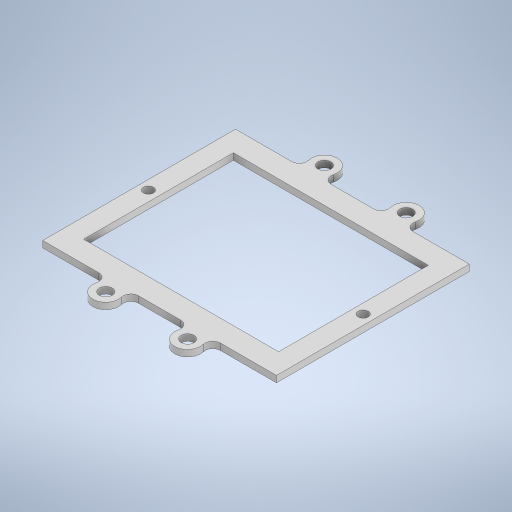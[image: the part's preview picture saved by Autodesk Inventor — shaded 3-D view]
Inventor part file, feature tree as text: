
AUTODESK INVENTOR PART (.ipt)
format: ipt  version: 2024 (Build 280153000, 153)  size: 338,944 bytes
history: native  units: in
note: dims shown in document units (in); Inventor stores cm internally (conversion verified against a paired STEP export)
features: extrude x3, plane x1, sketch x1
ambient origin geometry x8: Origin, YZ Plane, XZ Plane, XY Plane, X Axis, Y Axis, Z Axis, Center Point
bodies: Solid1 (feature_tree)
feature tree (5):
  plane  "Work Plane4"
  extrude  "Extrusion3"  Depth=0.1181in
  extrude  "Extrusion5"  Depth=0.1181in
  extrude  "Extrusion10"  Depth=0.1181in
  sketch  "Sketch9"  dims[d0=3.2874in d1=0.1181in d2=0.1181in d4=0.1969in d5=0.1969in d6=0.4724in d7=0.4724in d8=2.6575in d9=1.3287in d10=1.6437in d22=0.1181in d23=0.0in d24=0.3543in d27=0.185in d33=0.1181in d34=0.0in d43=3.9252in d44=0.1772in d87=0.0662in d90=1.2598in d92=0.3937in d94=2.7362in d96=3.563in d97=0.3543in d98=0.3543in d99=0.3937in d100=0.3937in d101=0.2362in d102=0.4724in d103=1.4961in d104=0.2756in d105=4.2717in d106=1.3878in d107=0.1181in d108=0.0in d31=0.0197in d32=0.0344in d91=0.0344in d93=0.0344in]
